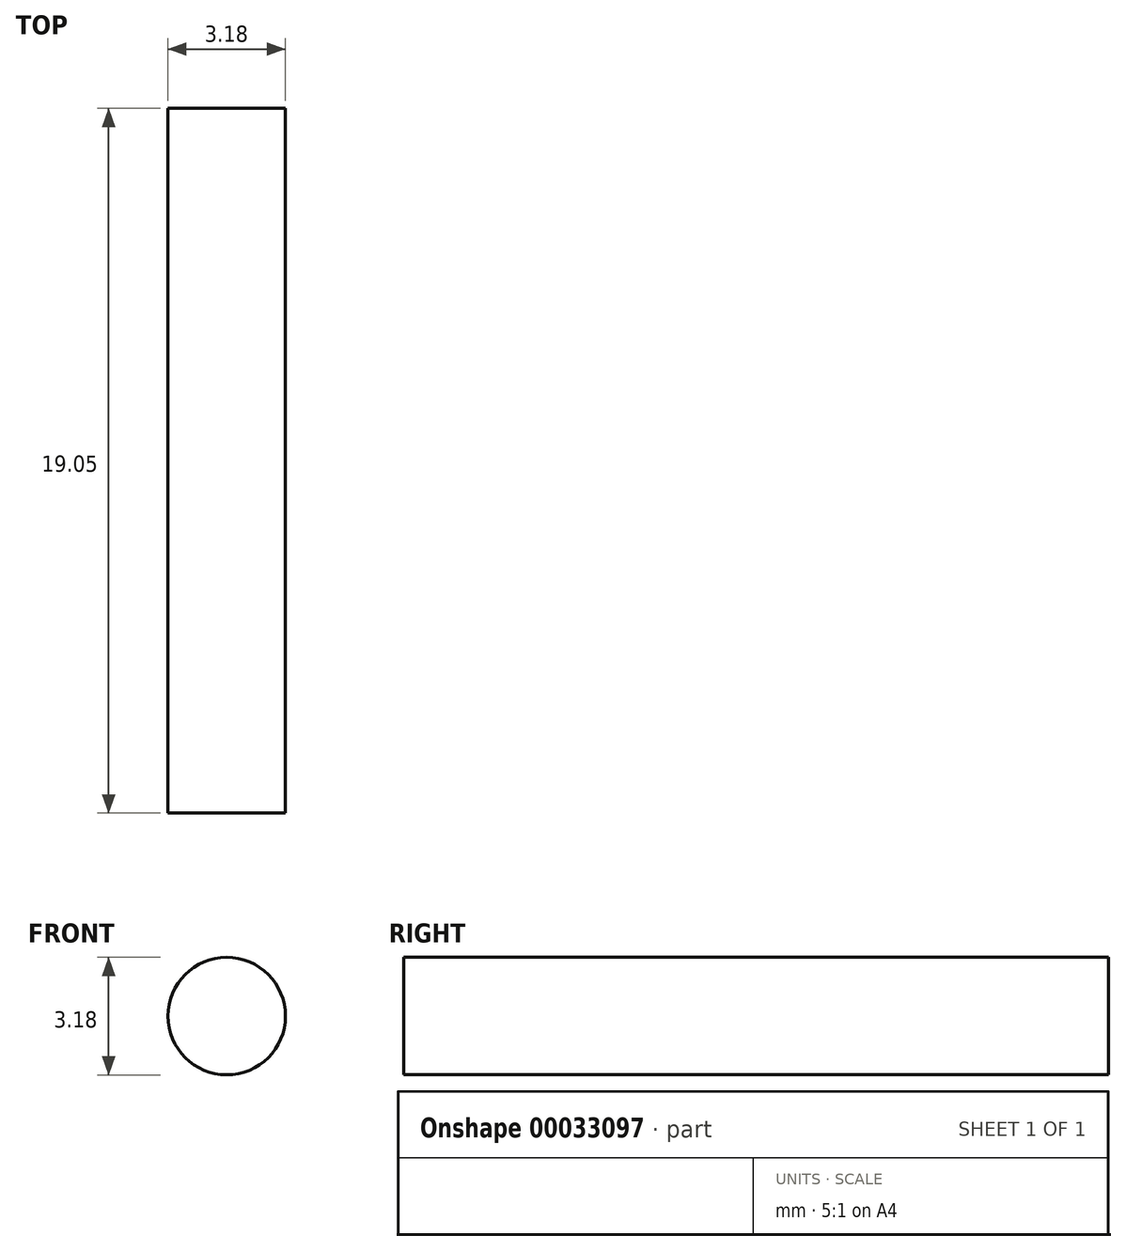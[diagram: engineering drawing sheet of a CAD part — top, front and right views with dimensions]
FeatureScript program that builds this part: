
annotation { "Feature Type Name" : "Feature", "Feature Type Description" : "" }
export const myFeature = defineFeature(function(context is Context, id is Id, definition is map)
    precondition{}
    {
        {
            var Q0;
            Q0=qCreatedBy(makeId("Front.planeOp"),FACE);
            var sketch = newSketch(context, id + "F0", { "sketchPlane" : qUnion([Q0])});
            skCircle(sketch, "E0", {"center": v(0, 0) * mm, "radius": 1.59 * mm});
            skSolve(sketch);
        }
        {
            var Q0;
            Q0 = qSketchRegion(id + "F0", true);
            extrude(context, id + "F1", {"entities" : qUnion([Q0]), "depth" : 19.05 * mm});
        }
    });
